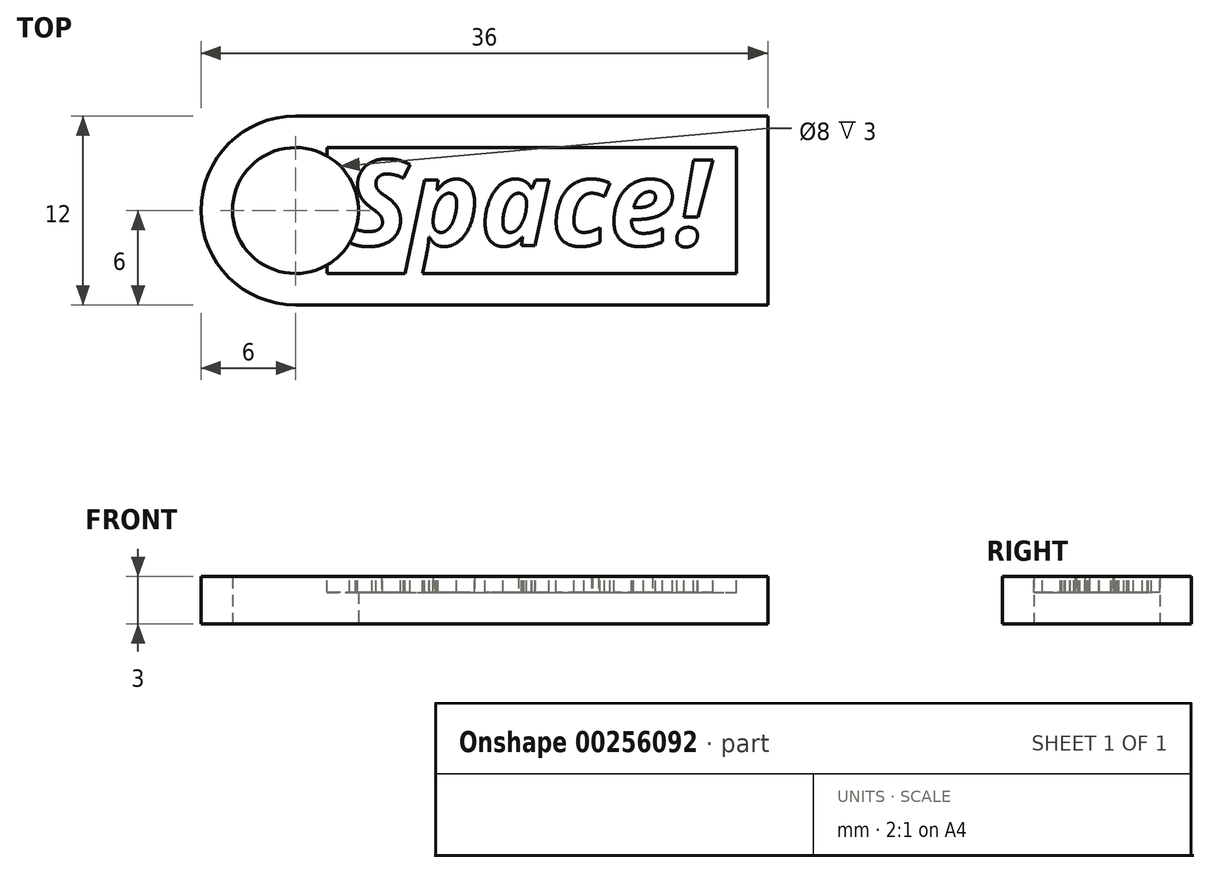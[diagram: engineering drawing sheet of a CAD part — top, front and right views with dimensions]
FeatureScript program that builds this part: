
annotation { "Feature Type Name" : "Feature", "Feature Type Description" : "" }
export const myFeature = defineFeature(function(context is Context, id is Id, definition is map)
    precondition{}
    {
        {
            var Q0;
            Q0=qCreatedBy(makeId("Top.planeOp"),FACE);
            var sketch = newSketch(context, id + "F0", { "sketchPlane" : qUnion([Q0])});
            skLineSegment(sketch, "E0.bottom", {"start": v(0, 0) * mm, "end": v(30, 0) * mm});
            skLineSegment(sketch, "E0.top", {"start": v(0, 12) * mm, "end": v(30, 12) * mm});
            skLineSegment(sketch, "E0.left", {"start": v(0, 0) * mm, "end": v(0, 12) * mm});
            skLineSegment(sketch, "E0.right", {"start": v(30, 0) * mm, "end": v(30, 12) * mm});
            skArc(sketch, "E1", {"start": v(0, 12) * mm, "mid": v(-6, 6) * mm, "end": v(0, 0) * mm});
            skCircle(sketch, "E2", {"center": v(0, 6) * mm, "radius": 4 * mm});
            skSolve(sketch);
        }
        {
            var Q0;
            {var subQ0=sQuery(id+"F0.wireOp",EDGE,"E1");Q0=makeQuery(id+"F0.imprint","IMPRINT",FACE,{"disambiguationData":[TD([[makeQuery(id+"F0.imprint","IMPRINT",EDGE,{"derivedFrom":subQ0}),1.0]])]});}
            var Q1;
            {var subQ5=sQuery(id+"F0.wireOp",EDGE,"E0.bottom");Q1=makeQuery(id+"F0.imprint","IMPRINT",FACE,{"disambiguationData":[TD([[makeQuery(id+"F0.imprint","IMPRINT",EDGE,{"derivedFrom":subQ5}),1.0]])]});}
            var Q2;
            {var subQ0=sQuery(id+"F0.wireOp",EDGE,"E2");var subQ1=sQuery(id+"F0.wireOp",EDGE,"E0.left");var subQ2=makeQuery(id+"F0.imprint","INTERSECT",VERTEX,{"disambiguationData":[OD(0.0)],"derivedFrom":[subQ1,subQ0]});Q2=makeQuery(id+"F0.imprint","IMPRINT",FACE,{"disambiguationData":[TD([[makeQuery(id+"F0.imprint","IMPRINT",EDGE,{"disambiguationData":[TD([[subQ2,-1.0]])],"derivedFrom":subQ1}),-1.0]])]});}
            extrude(context, id + "F1", {"entities" : qUnion([Q0, Q1, Q2]), "depth" : 3 * mm});
        }
        {
            var Q0;
            Q0=makeQuery(id+"F1.opExtrude","CAP_FACE",FACE,{"disambiguationData":[OSD([sQuery(id+"F0.wireOp",EDGE,"E0.bottom"),sQuery(id+"F0.wireOp",EDGE,"E0.top"),sQuery(id+"F0.wireOp",EDGE,"E0.left"),sQuery(id+"F0.wireOp",EDGE,"E0.right"),sQuery(id+"F0.wireOp",EDGE,"E1"),sQuery(id+"F0.wireOp",EDGE,"E2")])],"isStart":false});
            var sketch = newSketch(context, id + "F2", { "sketchPlane" : qUnion([Q0])});
            skLineSegment(sketch, "E3.bottom", {"start": v(2, 10) * mm, "end": v(28, 10) * mm});
            skLineSegment(sketch, "E3.top", {"start": v(2, 2) * mm, "end": v(28, 2) * mm});
            skLineSegment(sketch, "E3.left", {"start": v(2, 10) * mm, "end": v(2, 2) * mm});
            skLineSegment(sketch, "E3.right", {"start": v(28, 10) * mm, "end": v(28, 2) * mm});
            skText(sketch, "E4", { "text": "Space!", "fontName": "OpenSans-BoldItalic.ttf"});
            const initialGuessF2  = {"E4": [0.00316, 0.00378, 1, 0, 0.00547]};
            skSetInitialGuess(sketch, initialGuessF2);
            skSolve(sketch);
        }
        {
            var Q0;
            Q0=makeQuery(id+"F2.imprint","IMPRINT",FACE,{"disambiguationData":[TD([[makeQuery(id+"F2.imprint","IMPRINT",EDGE,{"derivedFrom":sQuery(id+"F2.wireOp",EDGE,"E3.bottom")}),-1.0]])]});
            var Q1;
            Q1=makeQuery(id+"F2.imprint","IMPRINT",FACE,{"disambiguationData":[TD([[makeQuery(id+"F2.imprint","IMPRINT",EDGE,{"derivedFrom":sQuery(id+"F2.wireOp",EDGE,"E4.sketch_text.stroke-40")}),1.0]])]});
            var Q2;
            Q2=makeQuery(id+"F2.imprint","IMPRINT",FACE,{"disambiguationData":[TD([[makeQuery(id+"F2.imprint","IMPRINT",EDGE,{"derivedFrom":sQuery(id+"F2.wireOp",EDGE,"E4.sketch_text.stroke-64")}),1.0]])]});
            var Q3;
            Q3=makeQuery(id+"F2.imprint","IMPRINT",FACE,{"disambiguationData":[TD([[makeQuery(id+"F2.imprint","IMPRINT",EDGE,{"derivedFrom":sQuery(id+"F2.wireOp",EDGE,"E4.sketch_text.stroke-92")}),1.0]])]});
            extrude(context, id + "F3", {"entities" : qUnion([Q0, Q1, Q2, Q3]), "oppositeDirection" : true, "depth" : 1 * mm});
        }
        {
            var Q0;
            Q0=makeQuery(id+"F3.opExtrude","SWEPT_BODY",BODY,{"disambiguationData":[OSD([sQuery(id+"F2.wireOp",EDGE,"E4.sketch_text.stroke-64"),sQuery(id+"F2.wireOp",EDGE,"E4.sketch_text.stroke-65"),sQuery(id+"F2.wireOp",EDGE,"E4.sketch_text.stroke-66"),sQuery(id+"F2.wireOp",EDGE,"E4.sketch_text.stroke-67"),sQuery(id+"F2.wireOp",EDGE,"E4.sketch_text.stroke-68"),sQuery(id+"F2.wireOp",EDGE,"E4.sketch_text.stroke-69"),sQuery(id+"F2.wireOp",EDGE,"E4.sketch_text.stroke-70"),sQuery(id+"F2.wireOp",EDGE,"E4.sketch_text.stroke-71"),sQuery(id+"F2.wireOp",EDGE,"E4.sketch_text.stroke-72"),sQuery(id+"F2.wireOp",EDGE,"E4.sketch_text.stroke-73")])]});
            var Q1;
            Q1=makeQuery(id+"F3.opExtrude","SWEPT_BODY",BODY,{"disambiguationData":[OSD([sQuery(id+"F2.wireOp",EDGE,"E4.sketch_text.stroke-40"),sQuery(id+"F2.wireOp",EDGE,"E4.sketch_text.stroke-41"),sQuery(id+"F2.wireOp",EDGE,"E4.sketch_text.stroke-42"),sQuery(id+"F2.wireOp",EDGE,"E4.sketch_text.stroke-43"),sQuery(id+"F2.wireOp",EDGE,"E4.sketch_text.stroke-44"),sQuery(id+"F2.wireOp",EDGE,"E4.sketch_text.stroke-45"),sQuery(id+"F2.wireOp",EDGE,"E4.sketch_text.stroke-46"),sQuery(id+"F2.wireOp",EDGE,"E4.sketch_text.stroke-47"),sQuery(id+"F2.wireOp",EDGE,"E4.sketch_text.stroke-48")])]});
            var Q2;
            Q2=makeQuery(id+"F3.opExtrude","SWEPT_BODY",BODY,{"disambiguationData":[OSD([sQuery(id+"F2.wireOp",EDGE,"E4.sketch_text.stroke-92"),sQuery(id+"F2.wireOp",EDGE,"E4.sketch_text.stroke-93"),sQuery(id+"F2.wireOp",EDGE,"E4.sketch_text.stroke-94"),sQuery(id+"F2.wireOp",EDGE,"E4.sketch_text.stroke-95"),sQuery(id+"F2.wireOp",EDGE,"E4.sketch_text.stroke-96"),sQuery(id+"F2.wireOp",EDGE,"E4.sketch_text.stroke-97")])]});
            var Q3;
            Q3=makeQuery(id+"F3.opExtrude","SWEPT_BODY",BODY,{"disambiguationData":[OSD([sQuery(id+"F2.wireOp",EDGE,"E3.bottom"),sQuery(id+"F2.wireOp",EDGE,"E3.top"),sQuery(id+"F2.wireOp",EDGE,"E3.left"),sQuery(id+"F2.wireOp",EDGE,"E3.right"),sQuery(id+"F2.wireOp",EDGE,"E4.sketch_text.stroke-0"),sQuery(id+"F2.wireOp",EDGE,"E4.sketch_text.stroke-1"),sQuery(id+"F2.wireOp",EDGE,"E4.sketch_text.stroke-2"),sQuery(id+"F2.wireOp",EDGE,"E4.sketch_text.stroke-3"),sQuery(id+"F2.wireOp",EDGE,"E4.sketch_text.stroke-4"),sQuery(id+"F2.wireOp",EDGE,"E4.sketch_text.stroke-5"),sQuery(id+"F2.wireOp",EDGE,"E4.sketch_text.stroke-6"),sQuery(id+"F2.wireOp",EDGE,"E4.sketch_text.stroke-7"),sQuery(id+"F2.wireOp",EDGE,"E4.sketch_text.stroke-8"),sQuery(id+"F2.wireOp",EDGE,"E4.sketch_text.stroke-9"),sQuery(id+"F2.wireOp",EDGE,"E4.sketch_text.stroke-10"),sQuery(id+"F2.wireOp",EDGE,"E4.sketch_text.stroke-11"),sQuery(id+"F2.wireOp",EDGE,"E4.sketch_text.stroke-12"),sQuery(id+"F2.wireOp",EDGE,"E4.sketch_text.stroke-13"),sQuery(id+"F2.wireOp",EDGE,"E4.sketch_text.stroke-14"),sQuery(id+"F2.wireOp",EDGE,"E4.sketch_text.stroke-15"),sQuery(id+"F2.wireOp",EDGE,"E4.sketch_text.stroke-16"),sQuery(id+"F2.wireOp",EDGE,"E4.sketch_text.stroke-17"),sQuery(id+"F2.wireOp",EDGE,"E4.sketch_text.stroke-18"),sQuery(id+"F2.wireOp",EDGE,"E4.sketch_text.stroke-19"),sQuery(id+"F2.wireOp",EDGE,"E4.sketch_text.stroke-20"),sQuery(id+"F2.wireOp",EDGE,"E4.sketch_text.stroke-21"),sQuery(id+"F2.wireOp",EDGE,"E4.sketch_text.stroke-22"),sQuery(id+"F2.wireOp",EDGE,"E4.sketch_text.stroke-23"),sQuery(id+"F2.wireOp",EDGE,"E4.sketch_text.stroke-24"),sQuery(id+"F2.wireOp",EDGE,"E4.sketch_text.stroke-25"),sQuery(id+"F2.wireOp",EDGE,"E4.sketch_text.stroke-26"),sQuery(id+"F2.wireOp",EDGE,"E4.sketch_text.stroke-27"),sQuery(id+"F2.wireOp",EDGE,"E4.sketch_text.stroke-28"),sQuery(id+"F2.wireOp",EDGE,"E4.sketch_text.stroke-29"),sQuery(id+"F2.wireOp",EDGE,"E4.sketch_text.stroke-30"),sQuery(id+"F2.wireOp",EDGE,"E4.sketch_text.stroke-31"),sQuery(id+"F2.wireOp",EDGE,"E4.sketch_text.stroke-32"),sQuery(id+"F2.wireOp",EDGE,"E4.sketch_text.stroke-33"),sQuery(id+"F2.wireOp",EDGE,"E4.sketch_text.stroke-35"),sQuery(id+"F2.wireOp",EDGE,"E4.sketch_text.stroke-36"),sQuery(id+"F2.wireOp",EDGE,"E4.sketch_text.stroke-37"),sQuery(id+"F2.wireOp",EDGE,"E4.sketch_text.stroke-38"),sQuery(id+"F2.wireOp",EDGE,"E4.sketch_text.stroke-39"),sQuery(id+"F2.wireOp",EDGE,"E4.sketch_text.stroke-49"),sQuery(id+"F2.wireOp",EDGE,"E4.sketch_text.stroke-50"),sQuery(id+"F2.wireOp",EDGE,"E4.sketch_text.stroke-51"),sQuery(id+"F2.wireOp",EDGE,"E4.sketch_text.stroke-52"),sQuery(id+"F2.wireOp",EDGE,"E4.sketch_text.stroke-53"),sQuery(id+"F2.wireOp",EDGE,"E4.sketch_text.stroke-54"),sQuery(id+"F2.wireOp",EDGE,"E4.sketch_text.stroke-55"),sQuery(id+"F2.wireOp",EDGE,"E4.sketch_text.stroke-56"),sQuery(id+"F2.wireOp",EDGE,"E4.sketch_text.stroke-57"),sQuery(id+"F2.wireOp",EDGE,"E4.sketch_text.stroke-58"),sQuery(id+"F2.wireOp",EDGE,"E4.sketch_text.stroke-59"),sQuery(id+"F2.wireOp",EDGE,"E4.sketch_text.stroke-60"),sQuery(id+"F2.wireOp",EDGE,"E4.sketch_text.stroke-61"),sQuery(id+"F2.wireOp",EDGE,"E4.sketch_text.stroke-62"),sQuery(id+"F2.wireOp",EDGE,"E4.sketch_text.stroke-63"),sQuery(id+"F2.wireOp",EDGE,"E4.sketch_text.stroke-74"),sQuery(id+"F2.wireOp",EDGE,"E4.sketch_text.stroke-75"),sQuery(id+"F2.wireOp",EDGE,"E4.sketch_text.stroke-76"),sQuery(id+"F2.wireOp",EDGE,"E4.sketch_text.stroke-77"),sQuery(id+"F2.wireOp",EDGE,"E4.sketch_text.stroke-78"),sQuery(id+"F2.wireOp",EDGE,"E4.sketch_text.stroke-79"),sQuery(id+"F2.wireOp",EDGE,"E4.sketch_text.stroke-80"),sQuery(id+"F2.wireOp",EDGE,"E4.sketch_text.stroke-81"),sQuery(id+"F2.wireOp",EDGE,"E4.sketch_text.stroke-82"),sQuery(id+"F2.wireOp",EDGE,"E4.sketch_text.stroke-83"),sQuery(id+"F2.wireOp",EDGE,"E4.sketch_text.stroke-84"),sQuery(id+"F2.wireOp",EDGE,"E4.sketch_text.stroke-85"),sQuery(id+"F2.wireOp",EDGE,"E4.sketch_text.stroke-86"),sQuery(id+"F2.wireOp",EDGE,"E4.sketch_text.stroke-87"),sQuery(id+"F2.wireOp",EDGE,"E4.sketch_text.stroke-88"),sQuery(id+"F2.wireOp",EDGE,"E4.sketch_text.stroke-89"),sQuery(id+"F2.wireOp",EDGE,"E4.sketch_text.stroke-90"),sQuery(id+"F2.wireOp",EDGE,"E4.sketch_text.stroke-91"),sQuery(id+"F2.wireOp",EDGE,"E4.sketch_text.stroke-98"),sQuery(id+"F2.wireOp",EDGE,"E4.sketch_text.stroke-99"),sQuery(id+"F2.wireOp",EDGE,"E4.sketch_text.stroke-100"),sQuery(id+"F2.wireOp",EDGE,"E4.sketch_text.stroke-101"),sQuery(id+"F2.wireOp",EDGE,"E4.sketch_text.stroke-102"),sQuery(id+"F2.wireOp",EDGE,"E4.sketch_text.stroke-103"),sQuery(id+"F2.wireOp",EDGE,"E4.sketch_text.stroke-104"),sQuery(id+"F2.wireOp",EDGE,"E4.sketch_text.stroke-105"),sQuery(id+"F2.wireOp",EDGE,"E4.sketch_text.stroke-106"),sQuery(id+"F2.wireOp",EDGE,"E4.sketch_text.stroke-107"),sQuery(id+"F2.wireOp",EDGE,"E4.sketch_text.stroke-108"),sQuery(id+"F2.wireOp",EDGE,"E4.sketch_text.stroke-109"),sQuery(id+"F2.wireOp",EDGE,"E4.sketch_text.stroke-110"),sQuery(id+"F2.wireOp",EDGE,"E4.sketch_text.stroke-111"),sQuery(id+"F2.wireOp",EDGE,"E4.sketch_text.stroke-112"),sQuery(id+"F2.wireOp",EDGE,"E4.sketch_text.stroke-113"),sQuery(id+"F2.wireOp",EDGE,"E4.sketch_text.stroke-114"),sQuery(id+"F2.wireOp",EDGE,"E4.sketch_text.stroke-115"),sQuery(id+"F2.wireOp",EDGE,"E4.sketch_text.stroke-116"),sQuery(id+"F2.wireOp",EDGE,"E4.sketch_text.stroke-117"),sQuery(id+"F2.wireOp",EDGE,"E4.sketch_text.stroke-118"),sQuery(id+"F2.wireOp",EDGE,"E4.sketch_text.stroke-119"),sQuery(id+"F2.wireOp",EDGE,"E4.sketch_text.stroke-120"),sQuery(id+"F2.wireOp",EDGE,"E4.sketch_text.stroke-121"),sQuery(id+"F2.wireOp",EDGE,"E4.sketch_text.stroke-122"),sQuery(id+"F2.wireOp",EDGE,"E4.sketch_text.stroke-123"),sQuery(id+"F2.wireOp",EDGE,"E4.sketch_text.stroke-124"),sQuery(id+"F2.wireOp",EDGE,"E4.sketch_text.stroke-125"),sQuery(id+"F2.wireOp",EDGE,"E4.sketch_text.stroke-126"),sQuery(id+"F2.wireOp",EDGE,"E4.sketch_text.stroke-127")])]});
            var Q4;
            Q4=makeQuery(id+"F1.opExtrude","SWEPT_BODY",BODY,{"disambiguationData":[OSD([sQuery(id+"F0.wireOp",EDGE,"E0.bottom"),sQuery(id+"F0.wireOp",EDGE,"E0.top"),sQuery(id+"F0.wireOp",EDGE,"E0.left"),sQuery(id+"F0.wireOp",EDGE,"E0.right"),sQuery(id+"F0.wireOp",EDGE,"E1"),sQuery(id+"F0.wireOp",EDGE,"E2")])]});
            booleanBodies(context, id + "F4", {"operationType" : BooleanOperationType.SUBTRACTION, "tools" : qUnion([Q0, Q1, Q2, Q3]), "targets" : qUnion([Q4])});
        }
    });
